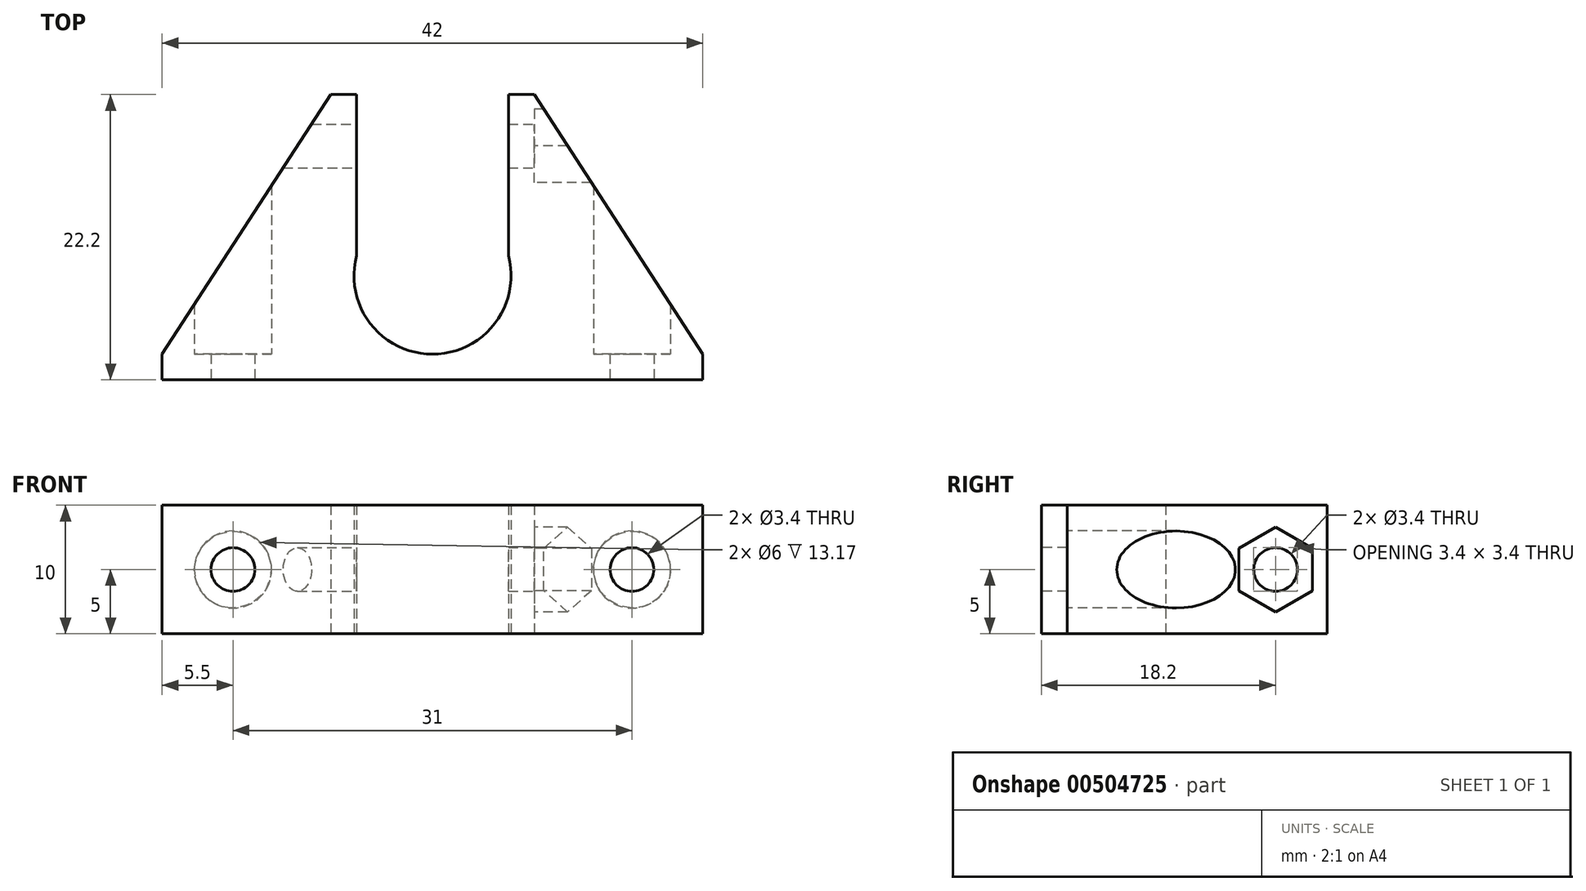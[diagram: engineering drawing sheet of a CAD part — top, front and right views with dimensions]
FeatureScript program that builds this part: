
annotation { "Feature Type Name" : "Feature", "Feature Type Description" : "" }
export const myFeature = defineFeature(function(context is Context, id is Id, definition is map)
    precondition{}
    {
        {
            var Q0;
            Q0=qCreatedBy(makeId("Top.planeOp"),FACE);
            var sketch = newSketch(context, id + "F0", { "sketchPlane" : qUnion([Q0])});
            skLineSegment(sketch, "E0", {"start": v(-21, 0) * mm, "end": v(21, 0) * mm});
            skLineSegment(sketch, "E1", {"start": v(-21, 0) * mm, "end": v(-21, 2) * mm});
            skLineSegment(sketch, "E2", {"start": v(-21, 2) * mm, "end": v(-7.9, 22.2) * mm});
            skLineSegment(sketch, "E3", {"start": v(-7.9, 22.2) * mm, "end": v(-5.9, 22.2) * mm});
            skLineSegment(sketch, "E4", {"start": v(7.9, 22.2) * mm, "end": v(21, 2) * mm});
            skLineSegment(sketch, "E5", {"start": v(21, 2) * mm, "end": v(21, 0) * mm});
            skArc(sketch, "E6", {"start": v(-5.9, 9.65) * mm, "mid": v(0, 2) * mm, "end": v(5.9, 9.65) * mm});
            skPoint(sketch, "E7", {"position": v(0, 22.2) * mm});
            skPoint(sketch, "E8", {"position": v(0, 2) * mm});
            skPoint(sketch, "E9", {"position": v(0, 14.2) * mm});
            skLineSegment(sketch, "E10", {"start": v(0, 22.2) * mm, "end": v(0, 14.2) * mm, "construction": true});
            skLineSegment(sketch, "E11", {"start": v(-10.5, 18.2) * mm, "end": v(10.5, 18.2) * mm, "construction": true});
            skPoint(sketch, "E12", {"position": v(0, 18.2) * mm});
            skLineSegment(sketch, "E13", {"start": v(-15.5, 0) * mm, "end": v(15.5, 0) * mm, "construction": true});
            skPoint(sketch, "E14", {"position": v(0, 0) * mm});
            skLineSegment(sketch, "E15", {"start": v(-15.5, 0) * mm, "end": v(-15.5, 18.2) * mm, "construction": true});
            skLineSegment(sketch, "E16", {"start": v(15.5, 0) * mm, "end": v(15.5, 18.2) * mm, "construction": true});
            skLineSegment(sketch, "E17", {"start": v(5.9, 9.65) * mm, "end": v(5.9, 22.2) * mm});
            skLineSegment(sketch, "E18", {"start": v(-5.9, 9.65) * mm, "end": v(-5.9, 22.2) * mm});
            skPoint(sketch, "E19", {"position": v(6.1, 8.1) * mm});
            skLineSegment(sketch, "E20.trimOffspring", {"start": v(5.9, 22.2) * mm, "end": v(7.9, 22.2) * mm});
            skSolve(sketch);
        }
        {
            var Q0;
            Q0=qSketchRegion(id+"F0",true);
            extrude(context, id + "F1", {"entities" : qUnion([Q0]), "endBound" : BoundingType.SYMMETRIC, "depth" : 10 * mm});
        }
        {
            var Q0;
            Q0=qCreatedBy(makeId("Front.planeOp"),FACE);
            var sketch = newSketch(context, id + "F2", { "sketchPlane" : qUnion([Q0])});
            skCircle(sketch, "E21", {"center": v(-15.5, 0) * mm, "radius": 1.7 * mm});
            skCircle(sketch, "E22", {"center": v(15.5, 0) * mm, "radius": 1.7 * mm});
            skSolve(sketch);
        }
        {
            var Q0;
            Q0=qSketchRegion(id+"F2",true);
            extrude(context, id + "F3", {"entities" : qUnion([Q0]), "operationType" : NewBodyOperationType.REMOVE, "endBound" : BoundingType.THROUGH_ALL, "oppositeDirection" : true, "depth" : 25 * mm});
        }
        {
            var Q0;
            Q0=qCreatedBy(makeId("Front.planeOp"),FACE);
            var Q1;
            Q1=sQuery(id+"F0.wireOp",VERTEX,"E2.start");
            cPlane(context, id + "F4", {"entities" : qUnion([Q0, Q1]), "cplaneType" : CPlaneType.PLANE_POINT, "offset" : 25 * mm, "width" : 150 * mm, "height" : 150 * mm});
        }
        {
            var Q0;
            Q0=qCreatedBy(id+"F4.planeOp",FACE);
            var sketch = newSketch(context, id + "F5", { "sketchPlane" : qUnion([Q0])});
            skCircle(sketch, "E23", {"center": v(-15.5, 0) * mm, "radius": 3 * mm});
            skCircle(sketch, "E24", {"center": v(15.5, 0) * mm, "radius": 3 * mm});
            skSolve(sketch);
        }
        {
            var Q0;
            Q0=qSketchRegion(id+"F5",true);
            extrude(context, id + "F6", {"entities" : qUnion([Q0]), "operationType" : NewBodyOperationType.REMOVE, "endBound" : BoundingType.THROUGH_ALL, "oppositeDirection" : true, "depth" : 25 * mm});
        }
        {
            var Q0;
            Q0=qCreatedBy(makeId("Right.planeOp"),FACE);
            var sketch = newSketch(context, id + "F7", { "sketchPlane" : qUnion([Q0])});
            skCircle(sketch, "E25", {"center": v(18.2, 0) * mm, "radius": 1.7 * mm});
            skSolve(sketch);
        }
        {
            var Q0;
            Q0=qSketchRegion(id+"F7",true);
            extrude(context, id + "F8", {"entities" : qUnion([Q0]), "operationType" : NewBodyOperationType.REMOVE, "endBound" : BoundingType.THROUGH_ALL, "oppositeDirection" : true, "depth" : 25 * mm, "hasSecondDirection" : true, "secondDirectionBound" : SecondDirectionBoundingType.THROUGH_ALL, "secondDirectionOppositeDirection" : false, "secondDirectionDepth" : 25 * mm});
        }
        {
            var Q0;
            Q0=qCreatedBy(makeId("Right.planeOp"),FACE);
            var Q1;
            Q1=sQuery(id+"F0.wireOp",VERTEX,"E4.start");
            cPlane(context, id + "F9", {"entities" : qUnion([Q0, Q1]), "cplaneType" : CPlaneType.PLANE_POINT, "offset" : 25 * mm, "width" : 150 * mm, "height" : 150 * mm});
        }
        {
            var Q0;
            Q0=qCreatedBy(id+"F9.planeOp",FACE);
            var sketch = newSketch(context, id + "F10", { "sketchPlane" : qUnion([Q0])});
            skCircle(sketch, "E26.cCircle", {"center": v(18.2, 0) * mm, "radius": 2.85 * mm, "construction": true});
            skLineSegment(sketch, "E26.0", {"start": v(21.05, -1.65) * mm, "end": v(18.2, -3.3) * mm});
            skLineSegment(sketch, "E26.1", {"start": v(18.2, -3.3) * mm, "end": v(15.35, -1.65) * mm});
            skLineSegment(sketch, "E26.2", {"start": v(15.35, -1.65) * mm, "end": v(15.35, 1.65) * mm});
            skLineSegment(sketch, "E26.3", {"start": v(15.35, 1.65) * mm, "end": v(18.2, 3.3) * mm});
            skLineSegment(sketch, "E26.4", {"start": v(18.2, 3.3) * mm, "end": v(21.05, 1.65) * mm});
            skLineSegment(sketch, "E26.5", {"start": v(21.05, 1.65) * mm, "end": v(21.05, -1.65) * mm});
            skPoint(sketch, "E26.0.midPoint", {"position": v(19.62, -2.47) * mm});
            skSolve(sketch);
        }
        {
            var Q0;
            Q0=qSketchRegion(id+"F10",true);
            extrude(context, id + "F11", {"entities" : qUnion([Q0]), "operationType" : NewBodyOperationType.REMOVE, "endBound" : BoundingType.THROUGH_ALL, "depth" : 25 * mm});
        }
    });
